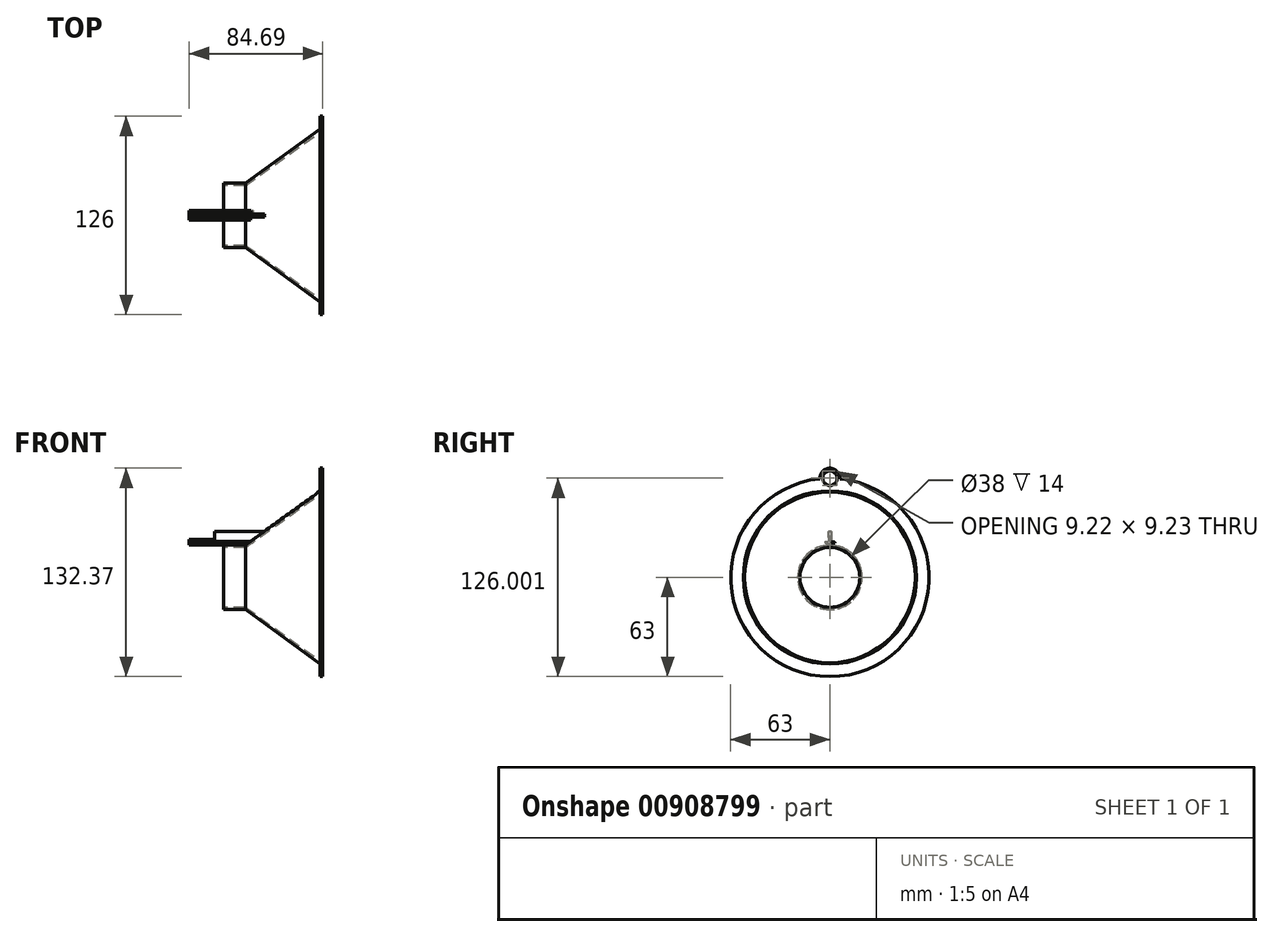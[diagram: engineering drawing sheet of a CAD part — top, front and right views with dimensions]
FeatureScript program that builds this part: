
annotation { "Feature Type Name" : "Feature", "Feature Type Description" : "" }
export const myFeature = defineFeature(function(context is Context, id is Id, definition is map)
    precondition{}
    {
        {
            var Q0;
            Q0=qCreatedBy(makeId("Front.planeOp"),FACE);
            var sketch = newSketch(context, id + "F0", { "sketchPlane" : qUnion([Q0])});
            skLineSegment(sketch, "E0", {"start": v(-188.79, 0) * mm, "end": v(333.35, 0) * mm, "construction": true});
            skLineSegment(sketch, "E1", {"start": v(0, 20.5) * mm, "end": v(14, 20.5) * mm});
            skLineSegment(sketch, "E2", {"start": v(14, 20.5) * mm, "end": v(59.26, 53.3) * mm});
            skLineSegment(sketch, "E3", {"start": v(63.01, 54.18) * mm, "end": v(14, 19) * mm});
            skLineSegment(sketch, "E4", {"start": v(14, 19) * mm, "end": v(0, 19) * mm});
            skLineSegment(sketch, "E5", {"start": v(0, 19) * mm, "end": v(0, 20.5) * mm});
            skLineSegment(sketch, "E6", {"start": v(63, 55) * mm, "end": v(63, 63) * mm});
            skLineSegment(sketch, "E7", {"start": v(63, 63) * mm, "end": v(61.5, 63) * mm});
            skLineSegment(sketch, "E8", {"start": v(61.5, 63) * mm, "end": v(61.5, 54.92) * mm});
            skLineSegment(sketch, "E9", {"start": v(59.26, 53.3) * mm, "end": v(61.5, 54.92) * mm});
            skLineSegment(sketch, "E10", {"start": v(63.01, 54.18) * mm, "end": v(63, 55) * mm});
            skSolve(sketch);
        }
        {
            var Q0;
            Q0=makeQuery(id+"F0.imprint","IMPRINT",FACE,{"disambiguationData":[TD([[makeQuery(id+"F0.imprint","IMPRINT",EDGE,{"derivedFrom":sQuery(id+"F0.wireOp",EDGE,"E1")}),-1.0]])]});
            var Q1;
            Q1=sQuery(id+"F0.wireOp",EDGE,"E0");
            revolve(context, id + "F1", {"surfaceOperationType" : NewSurfaceOperationType.NEW, "entities" : qUnion([Q0]), "axis" : qUnion([Q1]), "revolveType" : RevolveType.FULL});
        }
        {
            var Q0;
            Q0=makeQuery(id+"F1.opRevolve","SWEPT_FACE",FACE,{"disambiguationData":[OSD([sQuery(id+"F0.wireOp",EDGE,"E6")])]});
            var sketch = newSketch(context, id + "F2", { "sketchPlane" : qUnion([Q0])});
            skCircle(sketch, "E11", {"center": v(0, 63) * mm, "radius": 4.62 * mm});
            skCircle(sketch, "E12", {"center": v(0, 63) * mm, "radius": 6.37 * mm});
            skSolve(sketch);
        }
        {
            var Q0;
            {var subQ0=sQuery(id+"F2.wireOp",EDGE,"E11");var subQ1=makeQuery(id+"F1.opRevolve","SWEPT_EDGE",EDGE,{"disambiguationData":[OSD([sQuery(id+"F0.wireOp",EDGE,"E6"),sQuery(id+"F0.wireOp",EDGE,"E7")])]});var subQ2=makeQuery(id+"F2.imprint","INTERSECT",VERTEX,{"disambiguationData":[OD(0.0)],"derivedFrom":[subQ1,subQ0]});Q0=makeQuery(id+"F2.imprint","IMPRINT",FACE,{"disambiguationData":[TD([[makeQuery(id+"F2.imprint","IMPRINT",EDGE,{"disambiguationData":[TD([[subQ2,-1.0]])],"derivedFrom":subQ0}),-1.0]])]});}
            var Q1;
            {var subQ0=sQuery(id+"F2.wireOp",EDGE,"E11");var subQ1=makeQuery(id+"F1.opRevolve","SWEPT_EDGE",EDGE,{"disambiguationData":[OSD([sQuery(id+"F0.wireOp",EDGE,"E6"),sQuery(id+"F0.wireOp",EDGE,"E7")])]});var subQ2=makeQuery(id+"F2.imprint","INTERSECT",VERTEX,{"disambiguationData":[OD(0.0)],"derivedFrom":[subQ1,subQ0]});Q1=makeQuery(id+"F2.imprint","IMPRINT",FACE,{"disambiguationData":[TD([[makeQuery(id+"F2.imprint","IMPRINT",EDGE,{"disambiguationData":[TD([[subQ2,1.0]])],"derivedFrom":subQ0}),-1.0]])]});}
            extrude(context, id + "F3", {"entities" : qUnion([Q0, Q1]), "operationType" : NewBodyOperationType.ADD, "oppositeDirection" : true, "depth" : 1.5 * mm, "offsetDistance" : 25 * mm});
        }
        {
            var Q0;
            Q0=makeQuery(id+"F3.boolean.opBoolean","MERGE",FACE,{"derivedFrom":[makeQuery(id+"F1.opRevolve","SWEPT_FACE",FACE,{"disambiguationData":[OSD([sQuery(id+"F0.wireOp",EDGE,"E6")])]}),makeQuery(id+"F3.opExtrude","CAP_FACE",FACE,{"disambiguationData":[OSD([sQuery(id+"F2.wireOp",EDGE,"E11"),sQuery(id+"F2.wireOp",EDGE,"E12")])],"isStart":true})]});
            var sketch = newSketch(context, id + "F4", { "sketchPlane" : qUnion([Q0])});
            skCircle(sketch, "E13", {"center": v(0, 63) * mm, "radius": 4.61 * mm});
            skSolve(sketch);
        }
        {
            var Q0;
            Q0 = qSketchRegion(id + "F4", true);
            extrude(context, id + "F5", {"entities" : qUnion([Q0]), "operationType" : NewBodyOperationType.REMOVE, "endBound" : BoundingType.THROUGH_ALL, "oppositeDirection" : true, "depth" : 25 * mm, "offsetDistance" : 25 * mm});
        }
        {
            var Q0;
            Q0=qCreatedBy(makeId("Front.planeOp"),FACE);
            var sketch = newSketch(context, id + "F6", { "sketchPlane" : qUnion([Q0])});
            skLineSegment(sketch, "E14", {"start": v(26.02, 29.18) * mm, "end": v(-5.47, 29.18) * mm});
            skLineSegment(sketch, "E15", {"start": v(-5.47, 29.18) * mm, "end": v(-5.47, 24.23) * mm});
            skLineSegment(sketch, "E16", {"start": v(-5.47, 24.23) * mm, "end": v(-21.68, 24.23) * mm});
            skLineSegment(sketch, "E17", {"start": v(-21.68, 24.23) * mm, "end": v(-21.68, 20.5) * mm});
            skLineSegment(sketch, "E18", {"start": v(-21.68, 20.5) * mm, "end": v(0, 20.5) * mm});
            skLineSegment(sketch, "E19", {"start": v(26.02, 29.18) * mm, "end": v(14, 20.5) * mm});
            skLineSegment(sketch, "E20", {"start": v(14, 20.5) * mm, "end": v(0, 20.5) * mm});
            skSolve(sketch);
        }
        {
            var Q0;
            Q0=makeQuery(id+"F6.imprint","IMPRINT",FACE,{"disambiguationData":[TD([[makeQuery(id+"F6.imprint","IMPRINT",EDGE,{"derivedFrom":sQuery(id+"F6.wireOp",EDGE,"E14")}),1.0]])]});
            extrude(context, id + "F7", {"entities" : qUnion([Q0]), "operationType" : NewBodyOperationType.ADD, "endBound" : BoundingType.SYMMETRIC, "depth" : 2 * mm, "offsetDistance" : 25 * mm});
        }
        {
            var Q0;
            Q0=makeQuery(id+"F7.opExtrude","CAP_FACE",FACE,{"disambiguationData":[OSD([sQuery(id+"F6.wireOp",EDGE,"E14"),sQuery(id+"F6.wireOp",EDGE,"E15"),sQuery(id+"F6.wireOp",EDGE,"E16"),sQuery(id+"F6.wireOp",EDGE,"E17"),sQuery(id+"F6.wireOp",EDGE,"E18"),sQuery(id+"F6.wireOp",EDGE,"E19"),sQuery(id+"F6.wireOp",EDGE,"E20")])],"isStart":false});
            var sketch = newSketch(context, id + "F8", { "sketchPlane" : qUnion([Q0])});
            skLineSegment(sketch, "E21", {"start": v(-21.68, 22.93) * mm, "end": v(17.36, 22.93) * mm});
            skLineSegment(sketch, "E22", {"start": v(15.96, 21.92) * mm, "end": v(-21.68, 21.9) * mm});
            skLineSegment(sketch, "E23", {"start": v(-21.68, 21.9) * mm, "end": v(-21.68, 22.93) * mm});
            skLineSegment(sketch, "E24", {"start": v(15.96, 21.92) * mm, "end": v(17.36, 22.93) * mm});
            skSolve(sketch);
        }
        {
            var Q0;
            Q0=makeQuery(id+"F8.imprint","IMPRINT",FACE,{"disambiguationData":[TD([[makeQuery(id+"F8.imprint","IMPRINT",EDGE,{"derivedFrom":sQuery(id+"F8.wireOp",EDGE,"E21")}),-1.0]])]});
            extrude(context, id + "F9", {"entities" : qUnion([Q0]), "operationType" : NewBodyOperationType.ADD, "depth" : 2 * mm, "offsetDistance" : 25 * mm});
        }
        {
            var Q0;
            Q0=makeQuery(id+"F9.boolean.opBoolean","MERGE",FACE,{"derivedFrom":[makeQuery(id+"F7.opExtrude","SWEPT_FACE",FACE,{"disambiguationData":[OSD([sQuery(id+"F6.wireOp",EDGE,"E17")])]}),makeQuery(id+"F9.opExtrude","SWEPT_FACE",FACE,{"disambiguationData":[OSD([sQuery(id+"F8.wireOp",EDGE,"E23")])]})]});
            var sketch = newSketch(context, id + "F10", { "sketchPlane" : qUnion([Q0])});
            skLineSegment(sketch, "E25", {"start": v(-1, 22.92) * mm, "end": v(-3.28, 22.92) * mm});
            skLineSegment(sketch, "E26", {"start": v(-3.28, 22.92) * mm, "end": v(-3.28, 21.9) * mm});
            skLineSegment(sketch, "E27", {"start": v(-3.28, 21.9) * mm, "end": v(-1, 21.9) * mm});
            skSolve(sketch);
        }
        {
            var Q0;
            {var subQ0=sQuery(id+"F10.wireOp",EDGE,"E25");Q0=makeQuery(id+"F10.imprint","IMPRINT",FACE,{"disambiguationData":[TD([[makeQuery(id+"F10.imprint","IMPRINT",EDGE,{"derivedFrom":subQ0}),1.0]])]});}
            extrude(context, id + "F11", {"entities" : qUnion([Q0]), "operationType" : NewBodyOperationType.ADD, "oppositeDirection" : true, "depth" : 40.6 * mm, "offsetDistance" : 25 * mm});
        }
    });
